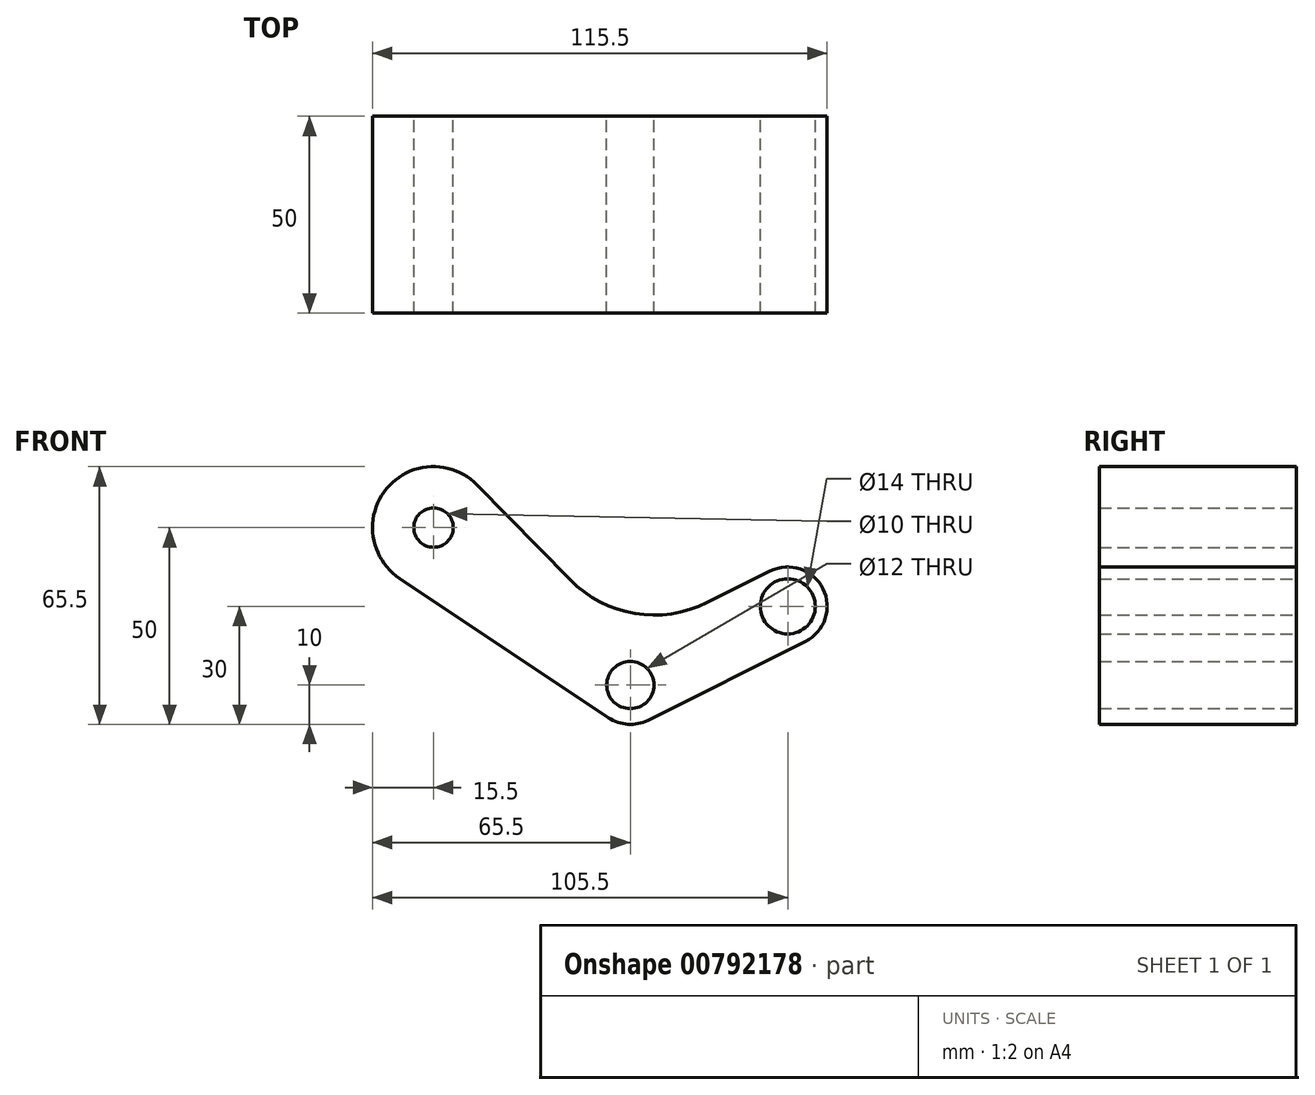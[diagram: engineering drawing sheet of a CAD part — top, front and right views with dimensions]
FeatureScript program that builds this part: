
annotation { "Feature Type Name" : "Feature", "Feature Type Description" : "" }
export const myFeature = defineFeature(function(context is Context, id is Id, definition is map)
    precondition{}
    {
        {
            var Q0;
            Q0=qCreatedBy(makeId("Front.planeOp"),FACE);
            var sketch = newSketch(context, id + "F0", { "sketchPlane" : qUnion([Q0])});
            skCircle(sketch, "E0", {"center": v(0, 0) * mm, "radius": 10 * mm});
            skCircle(sketch, "E1", {"center": v(0, 0) * mm, "radius": 6 * mm});
            skCircle(sketch, "E2", {"center": v(40, 20) * mm, "radius": 7 * mm});
            skCircle(sketch, "E3", {"center": v(40, 20) * mm, "radius": 10 * mm});
            skCircle(sketch, "E4", {"center": v(-50, 40) * mm, "radius": 5 * mm});
            skCircle(sketch, "E5", {"center": v(-50, 40) * mm, "radius": 15.5 * mm});
            skLineSegment(sketch, "E6", {"start": v(-5.55, -8.32) * mm, "end": v(-58.6, 27.1) * mm});
            skLineSegment(sketch, "E7", {"start": v(4.47, -8.94) * mm, "end": v(44.47, 11.06) * mm});
            skLineSegment(sketch, "E8", {"start": v(-38.94, 50.86) * mm, "end": v(-15.3, 26.77) * mm});
            skLineSegment(sketch, "E9", {"start": v(19.53, 20.95) * mm, "end": v(35.53, 28.94) * mm});
            skPoint(sketch, "E10.visualSharp", {"position": v(0, 11.18) * mm});
            skArc(sketch, "E10.filletArc", {"start": v(-15.3, 26.77) * mm, "mid": v(1.17, 18.19) * mm, "end": v(19.53, 20.95) * mm});
            skSolve(sketch);
        }
        {
            var Q0;
            Q0=makeQuery(id+"F0.imprint","IMPRINT",FACE,{"disambiguationData":[TD([[makeQuery(id+"F0.imprint","IMPRINT",EDGE,{"derivedFrom":sQuery(id+"F0.wireOp",EDGE,"E4")}),-1.0]])]});
            var Q1;
            {var subQ0=sQuery(id+"F0.wireOp",EDGE,"E6");Q1=makeQuery(id+"F0.imprint","IMPRINT",FACE,{"disambiguationData":[TD([[makeQuery(id+"F0.imprint","IMPRINT",EDGE,{"derivedFrom":subQ0}),-1.0]])]});}
            var Q2;
            Q2=makeQuery(id+"F0.imprint","IMPRINT",FACE,{"disambiguationData":[TD([[makeQuery(id+"F0.imprint","IMPRINT",EDGE,{"derivedFrom":sQuery(id+"F0.wireOp",EDGE,"E1")}),-1.0]])]});
            var Q3;
            Q3=makeQuery(id+"F0.imprint","IMPRINT",FACE,{"disambiguationData":[TD([[makeQuery(id+"F0.imprint","IMPRINT",EDGE,{"derivedFrom":sQuery(id+"F0.wireOp",EDGE,"E2")}),-1.0]])]});
            extrude(context, id + "F1", {"entities" : qUnion([Q0, Q1, Q2, Q3]), "endBound" : BoundingType.SYMMETRIC, "depth" : 50 * mm, "offsetDistance" : 25.4 * mm});
        }
    });
